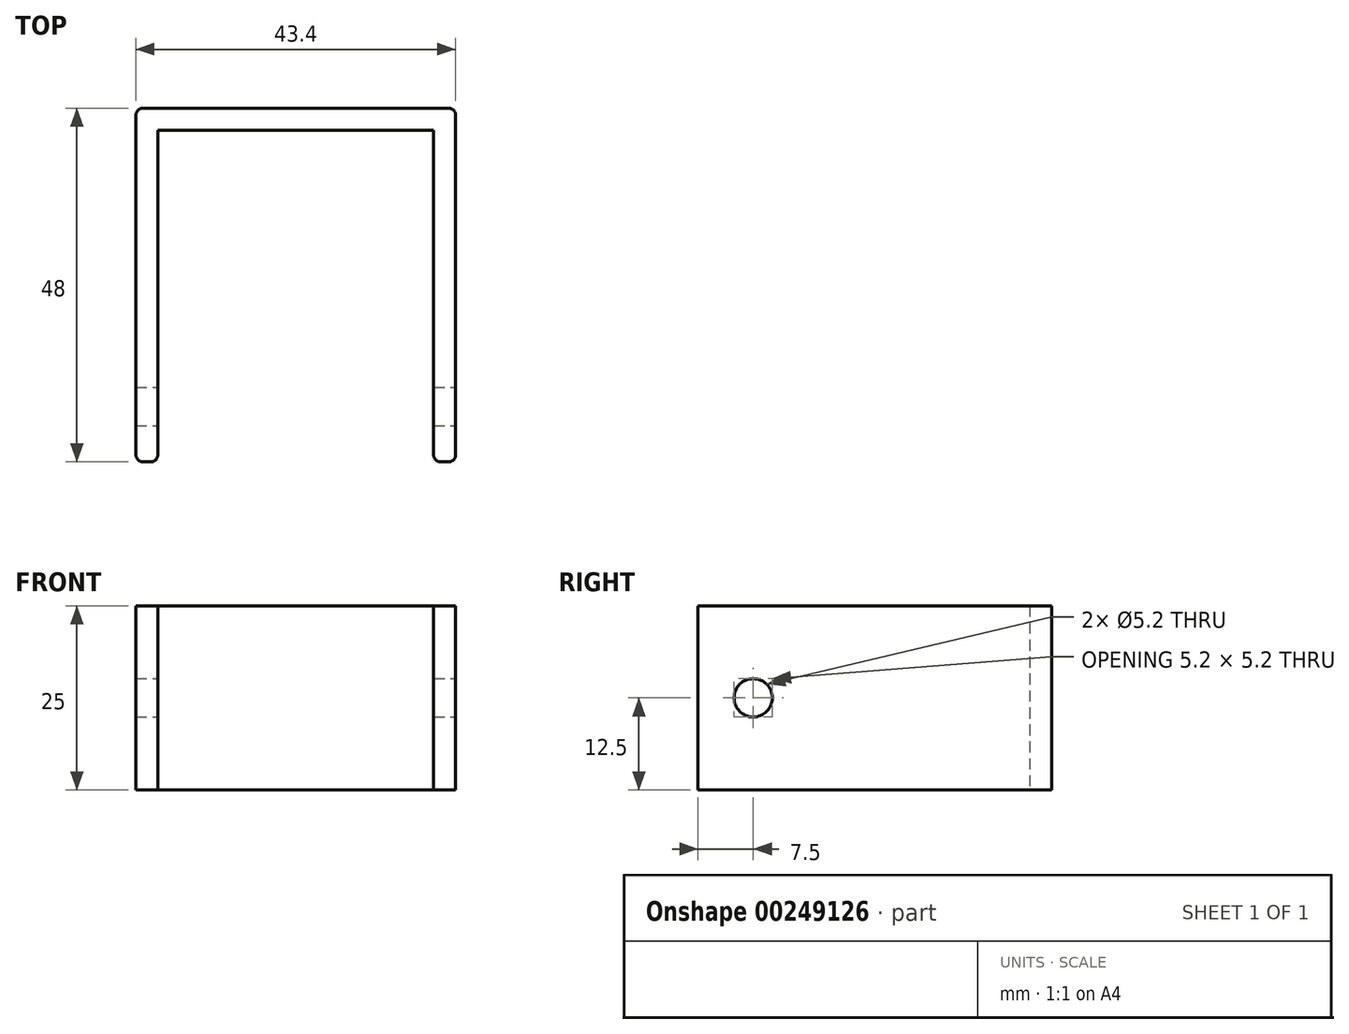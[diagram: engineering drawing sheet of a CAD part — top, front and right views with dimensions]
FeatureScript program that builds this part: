
annotation { "Feature Type Name" : "Feature", "Feature Type Description" : "" }
export const myFeature = defineFeature(function(context is Context, id is Id, definition is map)
    precondition{}
    {
        {
            var Q0;
            Q0=qCreatedBy(makeId("Top.planeOp"),FACE);
            var sketch = newSketch(context, id + "F0", { "sketchPlane" : qUnion([Q0])});
            skLineSegment(sketch, "E0", {"start": v(0, 0) * mm, "end": v(0, -48) * mm});
            skLineSegment(sketch, "E1", {"start": v(0, -48) * mm, "end": v(3, -48) * mm});
            skLineSegment(sketch, "E2", {"start": v(3, -48) * mm, "end": v(3, -3) * mm});
            skLineSegment(sketch, "E3", {"start": v(3, -3) * mm, "end": v(40.4, -3) * mm});
            skLineSegment(sketch, "E4", {"start": v(40.4, -3) * mm, "end": v(40.4, -48) * mm});
            skLineSegment(sketch, "E5", {"start": v(40.4, -48) * mm, "end": v(43.4, -48) * mm});
            skLineSegment(sketch, "E6", {"start": v(43.4, -48) * mm, "end": v(43.4, 0) * mm});
            skLineSegment(sketch, "E7", {"start": v(43.4, 0) * mm, "end": v(0, 0) * mm});
            skSolve(sketch);
        }
        {
            var Q0;
            Q0 = qSketchRegion(id + "F0", true);
            extrude(context, id + "F1", {"entities" : qUnion([Q0]), "depth" : 25 * mm});
        }
        {
            var Q0;
            Q0=makeQuery(id+"F1.opExtrude","SWEPT_FACE",FACE,{"disambiguationData":[OSD([sQuery(id+"F0.wireOp",EDGE,"E4")])]});
            var sketch = newSketch(context, id + "F2", { "sketchPlane" : qUnion([Q0])});
            skLineSegment(sketch, "E8", {"start": v(3, 25) * mm, "end": v(40.5, 25) * mm});
            skLineSegment(sketch, "E9", {"start": v(40.5, 25) * mm, "end": v(40.5, 12.5) * mm});
            skLineSegment(sketch, "E10", {"start": v(40.5, 12.5) * mm, "end": v(40.5, 0) * mm});
            skCircle(sketch, "E11", {"center": v(40.5, 12.5) * mm, "radius": 2.6 * mm});
            skSolve(sketch);
        }
        {
            var Q0;
            {var subQ0=sQuery(id+"F2.wireOp",EDGE,"E10");var subQ1=sQuery(id+"F2.wireOp",EDGE,"E9");var subQ2=makeQuery(id+"F2.imprint","INTERSECT",VERTEX,{"derivedFrom":[subQ1,subQ0]});Q0=makeQuery(id+"F2.imprint","IMPRINT",FACE,{"disambiguationData":[TD([[makeQuery(id+"F2.imprint","IMPRINT",EDGE,{"disambiguationData":[TD([[subQ2,1.0]])],"derivedFrom":subQ1}),-1.0]])]});}
            var Q1;
            {var subQ0=sQuery(id+"F2.wireOp",EDGE,"E10");var subQ1=sQuery(id+"F2.wireOp",EDGE,"E9");var subQ2=makeQuery(id+"F2.imprint","INTERSECT",VERTEX,{"derivedFrom":[subQ1,subQ0]});Q1=makeQuery(id+"F2.imprint","IMPRINT",FACE,{"disambiguationData":[TD([[makeQuery(id+"F2.imprint","IMPRINT",EDGE,{"disambiguationData":[TD([[subQ2,1.0]])],"derivedFrom":subQ1}),1.0]])]});}
            var Q2;
            Q2=sQuery(id+"F2.wireOp",EDGE,"E11");
            extrude(context, id + "F3", {"entities" : qUnion([Q0, Q1]), "operationType" : NewBodyOperationType.REMOVE, "surfaceEntities" : qUnion([Q2]), "endBound" : BoundingType.THROUGH_ALL, "depth" : 25 * mm, "hasSecondDirection" : true, "secondDirectionOppositeDirection" : true, "secondDirectionDepth" : 25 * mm});
        }
        {
            var Q0;
            Q0=makeQuery(id+"F1.opExtrude","SWEPT_EDGE",EDGE,{"disambiguationData":[OSD([sQuery(id+"F0.wireOp",EDGE,"E0"),sQuery(id+"F0.wireOp",EDGE,"E1")])]});
            var Q1;
            Q1=makeQuery(id+"F1.opExtrude","SWEPT_EDGE",EDGE,{"disambiguationData":[OSD([sQuery(id+"F0.wireOp",EDGE,"E1"),sQuery(id+"F0.wireOp",EDGE,"E2")])]});
            var Q2;
            Q2=makeQuery(id+"F1.opExtrude","SWEPT_EDGE",EDGE,{"disambiguationData":[OSD([sQuery(id+"F0.wireOp",EDGE,"E4"),sQuery(id+"F0.wireOp",EDGE,"E5")])]});
            var Q3;
            Q3=makeQuery(id+"F1.opExtrude","SWEPT_EDGE",EDGE,{"disambiguationData":[OSD([sQuery(id+"F0.wireOp",EDGE,"E5"),sQuery(id+"F0.wireOp",EDGE,"E6")])]});
            var Q4;
            Q4=makeQuery(id+"F1.opExtrude","SWEPT_EDGE",EDGE,{"disambiguationData":[OSD([sQuery(id+"F0.wireOp",EDGE,"E0"),sQuery(id+"F0.wireOp",EDGE,"E7")])]});
            fillet(context, id + "F4", {"entities" : qUnion([Q0, Q1, Q2, Q3, Q4]), "radius" : 1 * mm, "tangentPropagation" : true, "allowEdgeOverflow" : false});
        }
        {
            var Q0;
            Q0=makeQuery(id+"F1.opExtrude","SWEPT_EDGE",EDGE,{"disambiguationData":[OSD([sQuery(id+"F0.wireOp",EDGE,"E6"),sQuery(id+"F0.wireOp",EDGE,"E7")])]});
            fillet(context, id + "F5", {"entities" : qUnion([Q0]), "radius" : 1 * mm, "tangentPropagation" : true, "allowEdgeOverflow" : false});
        }
    });
